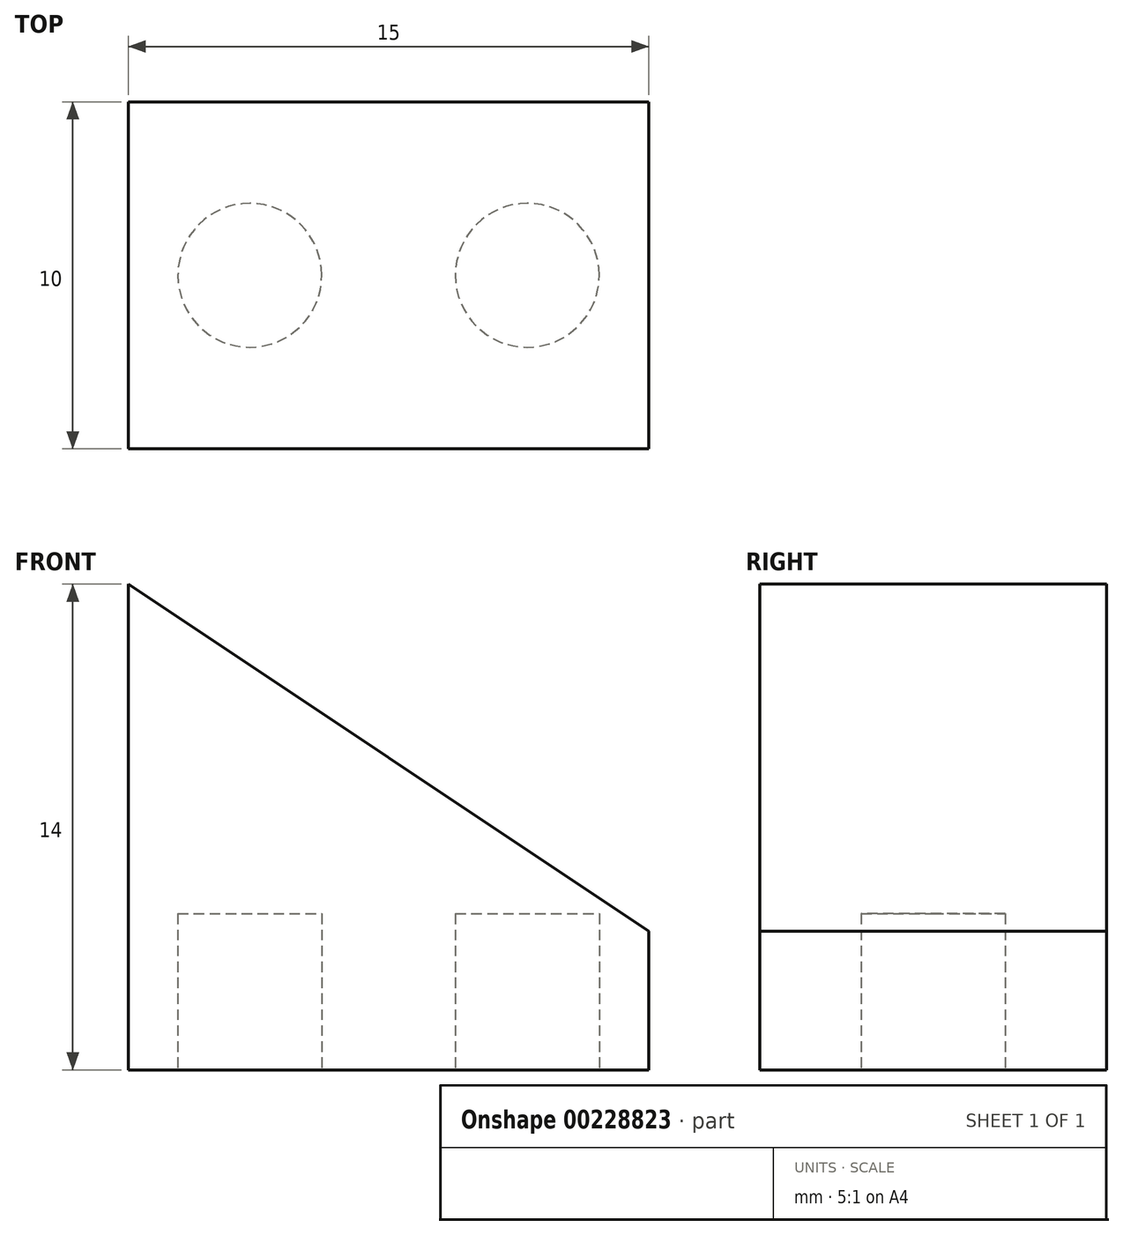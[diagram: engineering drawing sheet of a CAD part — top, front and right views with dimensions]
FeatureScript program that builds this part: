
annotation { "Feature Type Name" : "Feature", "Feature Type Description" : "" }
export const myFeature = defineFeature(function(context is Context, id is Id, definition is map)
    precondition{}
    {
        {
            var Q0;
            Q0=qCreatedBy(makeId("Front.planeOp"),FACE);
            var sketch = newSketch(context, id + "F0", { "sketchPlane" : qUnion([Q0])});
            skLineSegment(sketch, "E0", {"start": v(0, 14) * mm, "end": v(0, 0) * mm});
            skLineSegment(sketch, "E1", {"start": v(0, 0) * mm, "end": v(15, 0) * mm});
            skLineSegment(sketch, "E2", {"start": v(15, 4) * mm, "end": v(15, 0) * mm});
            skLineSegment(sketch, "E3", {"start": v(0, 14) * mm, "end": v(15, 4) * mm});
            skSolve(sketch);
        }
        {
            var Q0;
            Q0=makeQuery(id+"F0.imprint","IMPRINT",FACE,{"disambiguationData":[TD([[makeQuery(id+"F0.imprint","IMPRINT",EDGE,{"derivedFrom":sQuery(id+"F0.wireOp",EDGE,"E0")}),1.0]])]});
            extrude(context, id + "F1", {"entities" : qUnion([Q0]), "depth" : 5 * mm, "hasSecondDirection" : true, "secondDirectionOppositeDirection" : true, "secondDirectionDepth" : 5 * mm});
        }
        {
            var Q0;
            Q0=makeQuery(id+"F1.opExtrude","SWEPT_FACE",FACE,{"disambiguationData":[OSD([sQuery(id+"F0.wireOp",EDGE,"E1")])]});
            var sketch = newSketch(context, id + "F2", { "sketchPlane" : qUnion([Q0])});
            skCircle(sketch, "E4", {"center": v(3.5, 0) * mm, "radius": 2.07 * mm});
            skCircle(sketch, "E5", {"center": v(11.5, 0) * mm, "radius": 2.07 * mm});
            skLineSegment(sketch, "E6", {"start": v(0, 0) * mm, "end": v(7.5, 0) * mm, "construction": true});
            skLineSegment(sketch, "E7", {"start": v(3.5, 0) * mm, "end": v(11.5, 0) * mm, "construction": true});
            skLineSegment(sketch, "E8", {"start": v(7.5, 0) * mm, "end": v(7.5, 5) * mm, "construction": true});
            skSolve(sketch);
        }
        {
            var Q0;
            Q0=makeQuery(id+"F2.imprint","IMPRINT",FACE,{"disambiguationData":[TD([[makeQuery(id+"F2.imprint","IMPRINT",EDGE,{"derivedFrom":sQuery(id+"F2.wireOp",EDGE,"E4")}),1.0]])]});
            var Q1;
            Q1=makeQuery(id+"F2.imprint","IMPRINT",FACE,{"disambiguationData":[TD([[makeQuery(id+"F2.imprint","IMPRINT",EDGE,{"derivedFrom":sQuery(id+"F2.wireOp",EDGE,"E5")}),1.0]])]});
            extrude(context, id + "F3", {"entities" : qUnion([Q0, Q1]), "operationType" : NewBodyOperationType.REMOVE, "oppositeDirection" : true, "depth" : 4.5 * mm});
        }
    });
